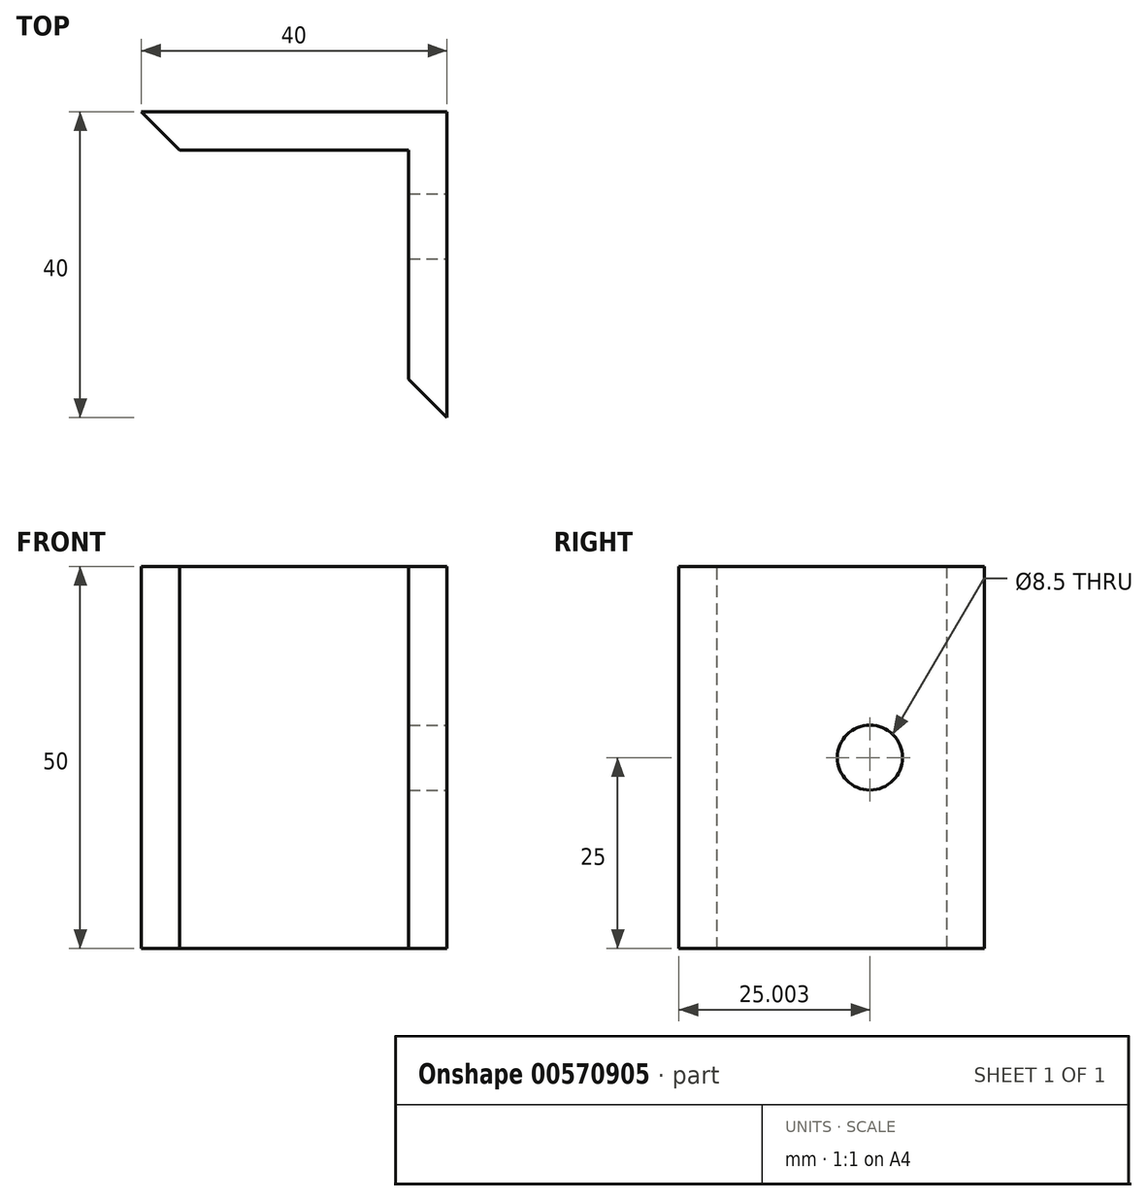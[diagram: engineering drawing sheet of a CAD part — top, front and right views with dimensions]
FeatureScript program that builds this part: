
annotation { "Feature Type Name" : "Feature", "Feature Type Description" : "" }
export const myFeature = defineFeature(function(context is Context, id is Id, definition is map)
    precondition{}
    {
        {
            var Q0;
            Q0=qCreatedBy(makeId("Top.planeOp"),FACE);
            var sketch = newSketch(context, id + "F0", { "sketchPlane" : qUnion([Q0])});
            skLineSegment(sketch, "E0", {"start": v(0, 23.61) * mm, "end": v(40, 23.61) * mm});
            skLineSegment(sketch, "E1", {"start": v(40, 23.61) * mm, "end": v(40, -16.39) * mm});
            skLineSegment(sketch, "E2", {"start": v(40, -16.39) * mm, "end": v(35, -16.39) * mm});
            skLineSegment(sketch, "E3", {"start": v(35, -16.39) * mm, "end": v(35, 18.61) * mm});
            skLineSegment(sketch, "E4", {"start": v(35, 18.61) * mm, "end": v(0, 18.61) * mm});
            skLineSegment(sketch, "E5", {"start": v(0, 18.61) * mm, "end": v(0, 23.61) * mm});
            skSolve(sketch);
        }
        {
            var Q0;
            Q0 = qSketchRegion(id + "F0", true);
            extrude(context, id + "F1", {"entities" : qUnion([Q0]), "depth" : 50 * mm, "offsetDistance" : 25 * mm});
        }
        {
            var Q0;
            Q0=makeQuery(id+"F1.opExtrude","SWEPT_EDGE",EDGE,{"disambiguationData":[OSD([sQuery(id+"F0.wireOp",EDGE,"E4"),sQuery(id+"F0.wireOp",EDGE,"E5")])]});
            var Q1;
            Q1=makeQuery(id+"F1.opExtrude","SWEPT_EDGE",EDGE,{"disambiguationData":[OSD([sQuery(id+"F0.wireOp",EDGE,"E2"),sQuery(id+"F0.wireOp",EDGE,"E3")])]});
            chamfer(context, id + "F2", {"entities" : qUnion([Q0, Q1]), "width" : 5 * mm, "tangentPropagation" : true});
        }
        {
            var Q0;
            Q0=makeQuery(id+"F1.opExtrude","SWEPT_FACE",FACE,{"disambiguationData":[OSD([sQuery(id+"F0.wireOp",EDGE,"E1")])]});
            var sketch = newSketch(context, id + "F3", { "sketchPlane" : qUnion([Q0])});
            skCircle(sketch, "E6", {"center": v(8.61, 25) * mm, "radius": 4.25 * mm});
            skSolve(sketch);
        }
        {
            var Q0;
            Q0 = qSketchRegion(id + "F3", true);
            extrude(context, id + "F4", {"entities" : qUnion([Q0]), "operationType" : NewBodyOperationType.REMOVE, "oppositeDirection" : true, "depth" : 25 * mm, "offsetDistance" : 25 * mm});
        }
    });
